# Revit family: Zumtobel TECTON BASIC LED
name_source: partatom
category: Lighting Fixtures
revit_build: Autodesk Revit 2016 (Build: 20150220_1215(x64)
units: mm (PartAtom-declared; Revit-internal decimal feet)

## family parameters
Cut with Voids When Loaded = No
Host = Face
Light Source = No
OmniClass Number = 23.80.70.11
OmniClass Title = Luminaries for Internal Lighting
Part Type = Normal
Room Calculation Point = No
Round Connector Dimension = Use Diameter
Shared = No

## types (1)
- TECTON B BASIC L1522 LED5200-840 LDE WH
    Apparent Load = 0 VA
    Assembly Code = D5020210
    Default Elevation = 0 mm  [stored 0 ft]
    Description = Continuous-row LED luminaire
    Fixture Type = Zumtobel TECTON BASIC LED (Lamp & Reflector) : L1522 47W LED Dimmable
    Length = 1522 mm  [stored 4.99344 ft]
    Manufacturer = Zumtobel Lighting
    Offset = 0 mm  [stored 0 ft]
    Track = Zumtobel_Metal_White
    URL = http://www.zumtobel.com
    Voltage = 230 V

note: [stored X ft] marks values corroborated as IEEE doubles in the binary element streams (Revit-internal decimal feet)

## geometry (parser evidence)
native form markers: Blend x33, Sweep x11
no freeform markers — native parametric forms only
